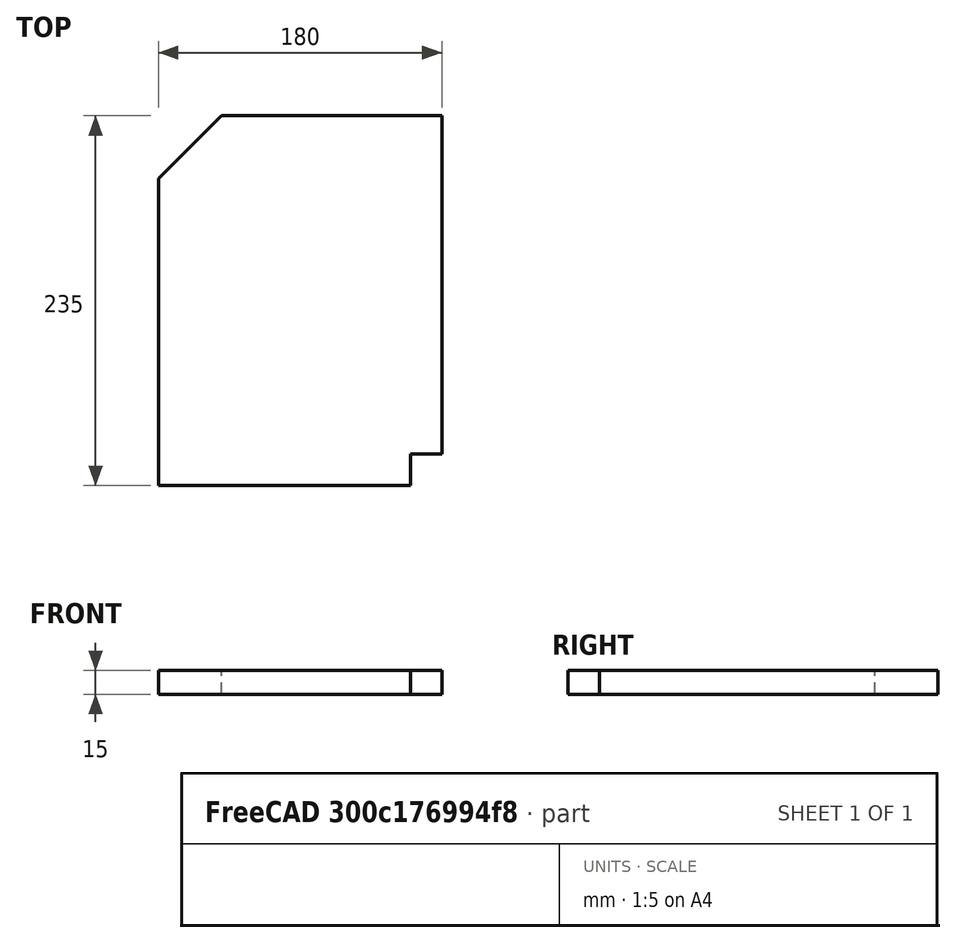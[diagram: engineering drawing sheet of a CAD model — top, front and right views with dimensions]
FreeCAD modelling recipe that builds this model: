
FCSTD DOCUMENT  (FreeCAD 0.18R4 (GitTag))
Label: RightSide-B
License: All rights reserved
LicenseURL: http://en.wikipedia.org/wiki/All_rights_reserved
objects: Sketcher::SketchObject×1, PartDesign::Pad×1, PartDesign::Body×1, App::Part×1
note: 4 computed .brp shape members not serialized (recipe doc carries the construction recipe); baked Part::Feature solids carry a one-line shape summary decoded from their .brp

FEATURE [Sketcher::SketchObject] CopySketch  label="Sketch"
  MapMode = 5
  Support = -> [XY_Plane001]
  sketch-geometry (7):
    g0: LineSegment StartX=-180 StartY=0 StartZ=0 EndX=-180 EndY=195 EndZ=0
    g1: LineSegment StartX=-180 StartY=195 StartZ=0 EndX=-140 EndY=235 EndZ=0
    g2: LineSegment StartX=-140 StartY=235 StartZ=0 EndX=0 EndY=235 EndZ=0
    g3: LineSegment StartX=-20 StartY=0 StartZ=0 EndX=-20 EndY=20 EndZ=0
    g4: LineSegment StartX=-20 StartY=20 StartZ=0 EndX=0 EndY=20 EndZ=0
    g5: LineSegment StartX=0 StartY=235 StartZ=0 EndX=0 EndY=20 EndZ=0
    g6: LineSegment StartX=-20 StartY=0 StartZ=0 EndX=-180 EndY=0 EndZ=0
  constraints (21):
    c: Coincident(g0,g1)
    c: Coincident(g1,g2)
    c: Vertical(g0)
    c: Horizontal(g2)
    c: Distance(g0) = 195
    c: Distance(g2) = 140
    c: Coincident(g3,g4)
    c: Vertical(g3)
    c: Horizontal(g4)
    c: Distance(g4) = 20
    c: Distance(g3) = 20
    c: Distance(g5) = 215
    c: Vertical(g5)
    c: Coincident(g2,g5)
    c: Horizontal(g6)
    c: Coincident(g0,g6)
    c: Coincident(g5,g4)
    c: Distance(g6) = 160
    c: Distance(g-1,g3) = 20
    c: Distance(g-1,g4) = 20
    c: Coincident(g6,g3)
FEATURE [PartDesign::Pad] Pad
  Length = 15
  Length2 = 100
  Profile = -> CopySketch
  Type = 0
FEATURE [PartDesign::Body] Body  label="Side"
  Group = -> [CopySketch,Pad]
  Origin = -> Origin001
  Tip = -> Pad
FEATURE [App::Part] Part
  Group = -> [Body]
  Origin = -> Origin
